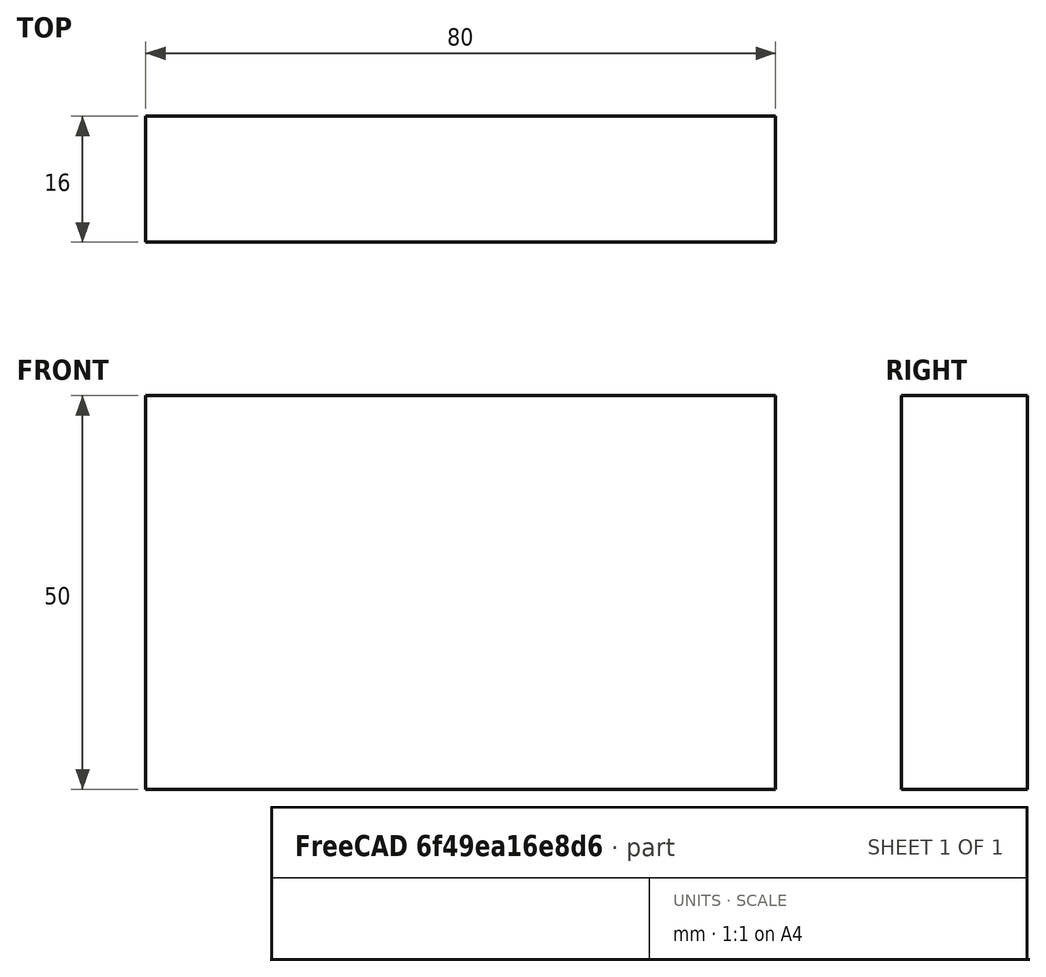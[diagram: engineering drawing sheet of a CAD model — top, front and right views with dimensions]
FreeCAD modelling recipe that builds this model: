
FCSTD DOCUMENT  (FreeCAD 0.15R4671 (Git))
Label: Flat Bar 80x16 EN10058 S235JR
License: All rights reserved
LicenseURL: http://en.wikipedia.org/wiki/All_rights_reserved
objects: Sketcher::SketchObject×1, Part::Extrusion×1
note: 2 computed .brp shape members not serialized (recipe doc carries the construction recipe); baked Part::Feature solids carry a one-line shape summary decoded from their .brp

FEATURE [Sketcher::SketchObject] Sketch
  sketch-geometry (4):
    g0: LineSegment StartX=-40 StartY=-8 StartZ=0 EndX=40 EndY=-8 EndZ=0
    g1: LineSegment StartX=40 StartY=-8 StartZ=0 EndX=40 EndY=8 EndZ=0
    g2: LineSegment StartX=40 StartY=8 StartZ=0 EndX=-40 EndY=8 EndZ=0
    g3: LineSegment StartX=-40 StartY=8 StartZ=0 EndX=-40 EndY=-8 EndZ=0
  constraints (12):
    c: Coincident(g0,g1)
    c: Coincident(g1,g2)
    c: Coincident(g2,g3)
    c: Coincident(g3,g0)
    c: Horizontal(g0)
    c: Horizontal(g2)
    c: Vertical(g1)
    c: Vertical(g3)
    c: Symmetric(g1,g2,g-2)
    c: Symmetric(g0,g1,g-1)
    c: DistanceY(g1) = 16
    c: DistanceX(g0) = 80
FEATURE [Part::Extrusion] Extrude  label="Flat Bar 80x16 EN10058 S235JR"
  Base = -> Sketch
  Dir = (0,0,50)
  Solid = true
